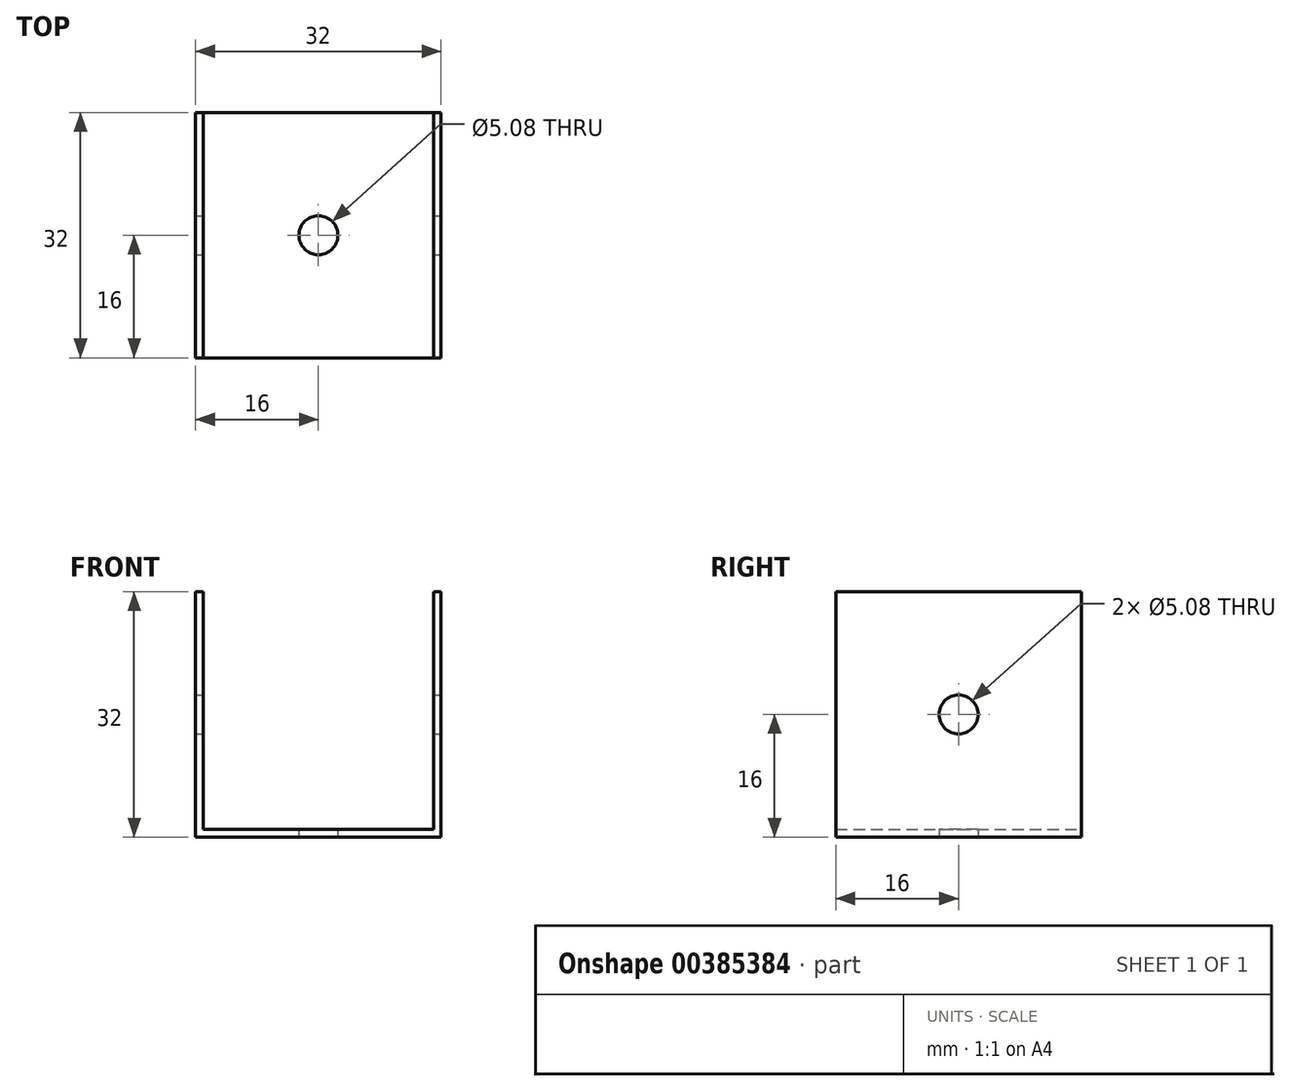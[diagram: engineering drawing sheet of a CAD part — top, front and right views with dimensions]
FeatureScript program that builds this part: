
annotation { "Feature Type Name" : "Feature", "Feature Type Description" : "" }
export const myFeature = defineFeature(function(context is Context, id is Id, definition is map)
    precondition{}
    {
        {
            var Q0;
            Q0=qCreatedBy(makeId("Front.planeOp"),FACE);
            var sketch = newSketch(context, id + "F0", { "sketchPlane" : qUnion([Q0])});
            skLineSegment(sketch, "E0", {"start": v(-16, 15.75) * mm, "end": v(-16, -16.25) * mm});
            skLineSegment(sketch, "E1", {"start": v(-16, -16.25) * mm, "end": v(16, -16.25) * mm});
            skLineSegment(sketch, "E2", {"start": v(16, -16.25) * mm, "end": v(16, 15.75) * mm});
            skLineSegment(sketch, "E3", {"start": v(16, 15.75) * mm, "end": v(15, 15.75) * mm});
            skLineSegment(sketch, "E4", {"start": v(15, 15.75) * mm, "end": v(15, -15.25) * mm});
            skLineSegment(sketch, "E5", {"start": v(15, -15.25) * mm, "end": v(-15, -15.25) * mm});
            skLineSegment(sketch, "E6", {"start": v(-15, -15.25) * mm, "end": v(-15, 15.75) * mm});
            skLineSegment(sketch, "E7", {"start": v(-15, 15.75) * mm, "end": v(-16, 15.75) * mm});
            skSolve(sketch);
        }
        {
            var Q0;
            Q0 = qSketchRegion(id + "F0", true);
            extrude(context, id + "F1", {"entities" : qUnion([Q0]), "depth" : 32 * mm});
        }
        {
            var Q0;
            Q0=makeQuery(id+"F1.opExtrude","SWEPT_FACE",FACE,{"disambiguationData":[OSD([sQuery(id+"F0.wireOp",EDGE,"E2")])]});
            var sketch = newSketch(context, id + "F2", { "sketchPlane" : qUnion([Q0])});
            skPoint(sketch, "E8", {"position": v(-16, -0.25) * mm});
            skCircle(sketch, "E9", {"center": v(-16, -0.25) * mm, "radius": 2.54 * mm});
            skSolve(sketch);
        }
        {
            var Q0;
            Q0=makeQuery(id+"F2.imprint","IMPRINT",FACE,{"disambiguationData":[TD([[makeQuery(id+"F2.imprint","IMPRINT",EDGE,{"derivedFrom":sQuery(id+"F2.wireOp",EDGE,"E9")}),1.0]])]});
            extrude(context, id + "F3", {"entities" : qUnion([Q0]), "operationType" : NewBodyOperationType.REMOVE, "oppositeDirection" : true, "depth" : 228.6 * mm});
        }
        {
            var Q0;
            Q0=makeQuery(id+"F1.opExtrude","SWEPT_FACE",FACE,{"disambiguationData":[OSD([sQuery(id+"F0.wireOp",EDGE,"E1")])]});
            var sketch = newSketch(context, id + "F4", { "sketchPlane" : qUnion([Q0])});
            skLineSegment(sketch, "E10", {"start": v(-16, 32) * mm, "end": v(16, 0) * mm});
            skLineSegment(sketch, "E11", {"start": v(16, 0) * mm, "end": v(-16, 32) * mm, "construction": true});
            skLineSegment(sketch, "E12", {"start": v(-16, 0) * mm, "end": v(16, 32) * mm, "construction": true});
            skPoint(sketch, "E13", {"position": v(0, 16) * mm});
            skCircle(sketch, "E14", {"center": v(0, 16) * mm, "radius": 2.54 * mm});
            skSolve(sketch);
        }
        {
            var Q0;
            {var subQ0=sQuery(id+"F4.wireOp",EDGE,"E14");var subQ1=sQuery(id+"F4.wireOp",EDGE,"E10");var subQ2=makeQuery(id+"F4.imprint","INTERSECT",VERTEX,{"disambiguationData":[OD(0.0)],"derivedFrom":[subQ1,subQ0]});Q0=makeQuery(id+"F4.imprint","IMPRINT",FACE,{"disambiguationData":[TD([[makeQuery(id+"F4.imprint","IMPRINT",EDGE,{"disambiguationData":[TD([[subQ2,-1.0]])],"derivedFrom":subQ1}),-1.0]])]});}
            var Q1;
            {var subQ0=sQuery(id+"F4.wireOp",EDGE,"E14");var subQ1=sQuery(id+"F4.wireOp",EDGE,"E10");var subQ2=makeQuery(id+"F4.imprint","INTERSECT",VERTEX,{"disambiguationData":[OD(0.0)],"derivedFrom":[subQ1,subQ0]});Q1=makeQuery(id+"F4.imprint","IMPRINT",FACE,{"disambiguationData":[TD([[makeQuery(id+"F4.imprint","IMPRINT",EDGE,{"disambiguationData":[TD([[subQ2,-1.0]])],"derivedFrom":subQ1}),1.0]])]});}
            extrude(context, id + "F5", {"entities" : qUnion([Q0, Q1]), "operationType" : NewBodyOperationType.REMOVE, "oppositeDirection" : true, "depth" : 76.2 * mm});
        }
    });
